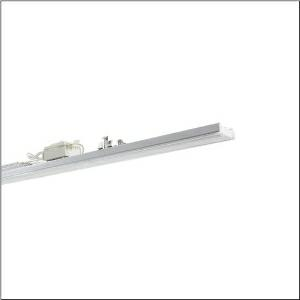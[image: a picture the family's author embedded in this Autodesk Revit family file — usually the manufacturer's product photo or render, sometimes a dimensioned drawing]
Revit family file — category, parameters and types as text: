
# Revit family: licross_r__11_recessed_mo_51te18dn695g_64c8
name_source: partatom
category: Lighting Fixtures
units: mm (PartAtom-declared; Revit-internal decimal feet)

## family parameters
Cut with Voids When Loaded = No
Host = Face
Light Source = No
Part Type = Normal
Room Calculation Point = No
Round Connector Dimension = Use Diameter
Shared = No

## types (1)
- --- (1 x LED, 9710 lm, 56.7 W, 6500K)
    Apparent Load = 57 VA
    CIE Flux Codes = 83 96 99 100 100
    Color Rendering = 80
    Color Temperature = 6500K
    Default Elevation = 1800 mm
    Description = Licross® 11 Recessed MO, luminaire insert, of sheet steel, galvanised, coil coated, white, length: 1.500mm, width: 66mm, height: 67mm, LED rated luminous flux: 9.710lm, light colour: 865, control gear: DALI 2, with plug, 5-pole, with phase selection, mains connection: 220..240V, AC, 50/60Hz, rated input power: 57W, halogen-free wiring, primary light control with lens, of plastic, primary optical cover: cover, of PMMA, light emission: direct distribution, primary light characteristic: symmetric, protection rating (complete): IP54, insulation class (complete): insulation class I (protective earthing), certification: CE, ENEC, VDE, UKCA, protection symbol: D if used in an environment with non-conductive dust loads with corresponding accessories, impact resistance: IK06, permissible ambient temperature for indoor applications: -25..+35°C, corresponds to IFS (International Featured Standards) requirements for safety and quality in the food industry, reducing of maximum allowable ambient temperature of 5°C with ceiling mounting, LABS conformity tested according to VDMA 24364:2018-05, packaging unit: 1 piece
    Height = 58 mm
    Lamp = 1 x LED
    Lamp Light Flux = 9710 lm
    Lamp Power = 56.7 W
    Lamp count = 1
    Length = 1500 mm
    Luminous efficacy = 171 lm/W
    Manufacturer = Siteco
    ModVariant = No
    Model = 51TE18DN695G
    Mounting Place = Ceiling
    Mounting Type = Pendant
    Number of Poles = 1
    OnlyDefault = Yes
    Power Factor = 1
    Product Name = Licross® 11 Recessed MO
    Product group = luminaire insert
    ProductGroupID = 902
    Protection Class = Protection class I
    Protection Degree = IP 54
    RLX_Detail_Level = 1
    RLX_Emergency_Light_Flux = 0 lm
    RLX_Emergency_Type = 0
    RLX_Emergency_Type_DB = No
    RlxData = <blob elided: 24465 chars, md5=e1002e9b>
    Socket = socket
    Standby Power = 0 W
    System Light Flux = 9710 lm
    System Power = 57 W
    Type Comments = factory setting: luminous flux: 100 % | dim-lin: 254 | 378 mA
    Type Image = l_1296930.jpg
    URL = http://relux.com
    VarID = @adj_010639
    Voltage = 0 V
    Weight = 0.00 kg
    Width = 66 mm

## geometry (parser evidence)
native form markers: Blend x4, Sweep x11
no freeform markers — native parametric forms only
